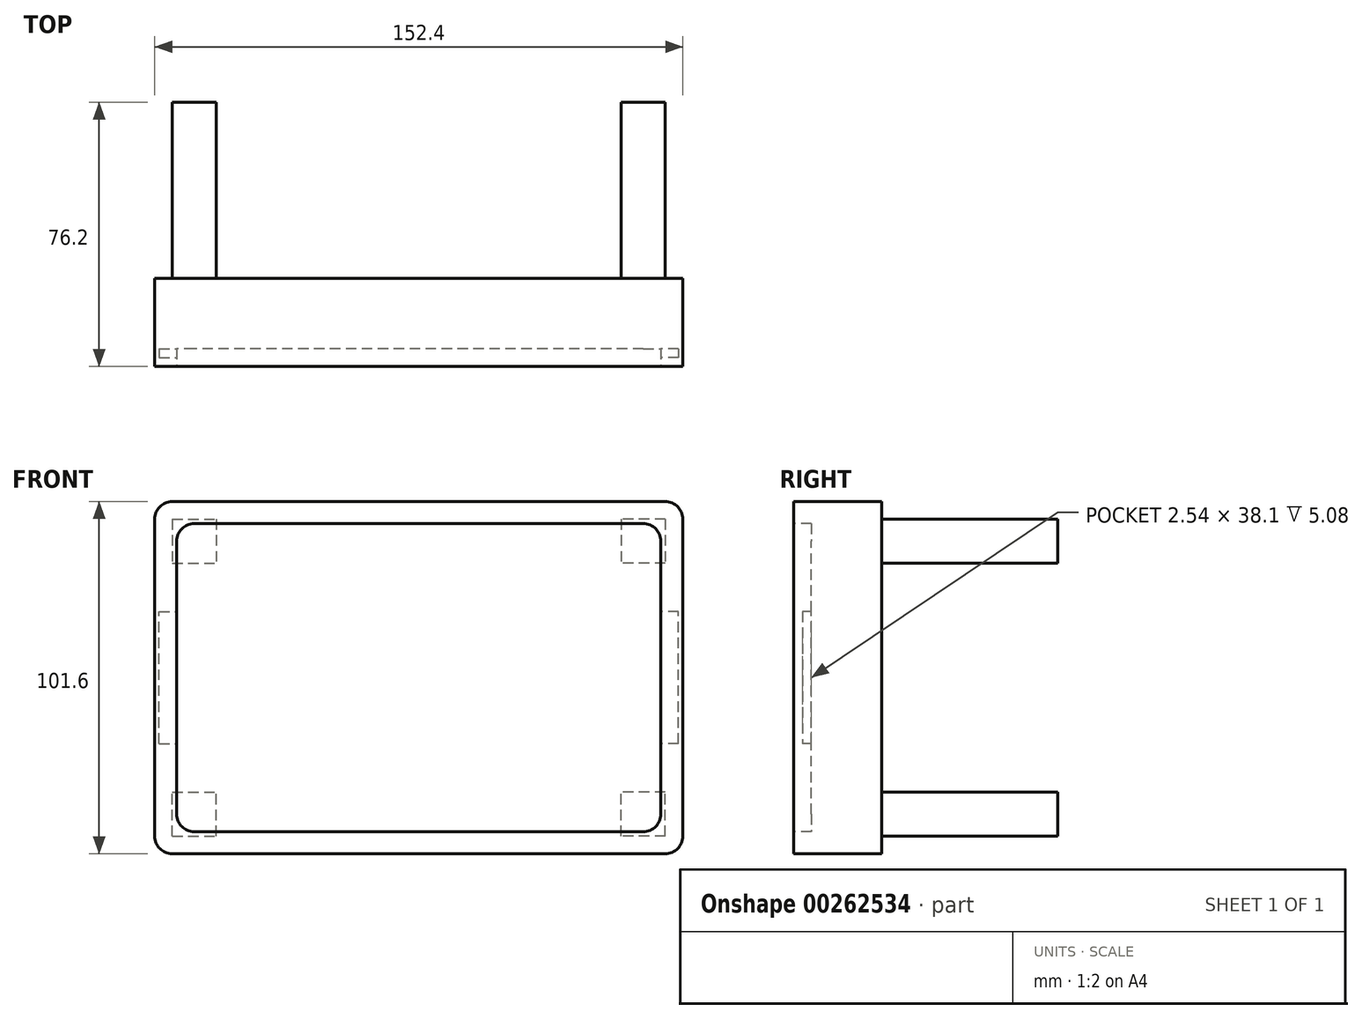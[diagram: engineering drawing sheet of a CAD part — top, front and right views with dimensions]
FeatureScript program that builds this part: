
annotation { "Feature Type Name" : "Feature", "Feature Type Description" : "" }
export const myFeature = defineFeature(function(context is Context, id is Id, definition is map)
    precondition{}
    {
        {
            var Q0;
            Q0=qCreatedBy(makeId("Front.planeOp"),FACE);
            var sketch = newSketch(context, id + "F0", { "sketchPlane" : qUnion([Q0])});
            skLineSegment(sketch, "E0.bottom", {"start": v(76.2, -50.8) * mm, "end": v(-76.2, -50.8) * mm});
            skLineSegment(sketch, "E0.top", {"start": v(76.2, 50.8) * mm, "end": v(-76.2, 50.8) * mm});
            skLineSegment(sketch, "E0.left", {"start": v(76.2, -50.8) * mm, "end": v(76.2, 50.8) * mm});
            skLineSegment(sketch, "E0.right", {"start": v(-76.2, -50.8) * mm, "end": v(-76.2, 50.8) * mm});
            skPoint(sketch, "E0.middle", {"position": v(0, 0) * mm});
            skSolve(sketch);
        }
        {
            var Q0;
            Q0=makeQuery(id+"F0.imprint","IMPRINT",FACE,{"disambiguationData":[TD([[makeQuery(id+"F0.imprint","IMPRINT",EDGE,{"derivedFrom":sQuery(id+"F0.wireOp",EDGE,"E0.bottom")}),-1.0]])]});
            extrude(context, id + "F1", {"entities" : qUnion([Q0]), "endBound" : BoundingType.SYMMETRIC, "depth" : 25.4 * mm});
        }
        {
            var Q0;
            Q0=makeQuery(id+"F1.opExtrude","CAP_FACE",FACE,{"disambiguationData":[OSD([sQuery(id+"F0.wireOp",EDGE,"E0.bottom"),sQuery(id+"F0.wireOp",EDGE,"E0.top"),sQuery(id+"F0.wireOp",EDGE,"E0.left"),sQuery(id+"F0.wireOp",EDGE,"E0.right")])],"isStart":false});
            var sketch = newSketch(context, id + "F2", { "sketchPlane" : qUnion([Q0])});
            skLineSegment(sketch, "E1.bottom", {"start": v(69.85, -44.45) * mm, "end": v(-69.85, -44.45) * mm});
            skLineSegment(sketch, "E1.top", {"start": v(69.85, 44.45) * mm, "end": v(-69.85, 44.45) * mm});
            skLineSegment(sketch, "E1.left", {"start": v(69.85, -44.45) * mm, "end": v(69.85, 44.45) * mm});
            skLineSegment(sketch, "E1.right", {"start": v(-69.85, -44.45) * mm, "end": v(-69.85, 44.45) * mm});
            skPoint(sketch, "E1.middle", {"position": v(0, 0) * mm});
            skSolve(sketch);
        }
        {
            var Q0;
            Q0=makeQuery(id+"F2.imprint","IMPRINT",FACE,{"disambiguationData":[TD([[makeQuery(id+"F2.imprint","IMPRINT",EDGE,{"derivedFrom":sQuery(id+"F2.wireOp",EDGE,"E1.bottom")}),-1.0]])]});
            extrude(context, id + "F3", {"entities" : qUnion([Q0]), "operationType" : NewBodyOperationType.REMOVE, "oppositeDirection" : true, "depth" : 5.08 * mm});
        }
        {
            var Q0;
            Q0=makeQuery(id+"F3.boolean.opBoolean","COPY",EDGE,{"derivedFrom":makeQuery(id+"F3.opExtrude","SWEPT_EDGE",EDGE,{"disambiguationData":[OSD([sQuery(id+"F2.wireOp",EDGE,"E1.bottom"),sQuery(id+"F2.wireOp",EDGE,"E1.right")])]})});
            var Q1;
            Q1=makeQuery(id+"F3.boolean.opBoolean","COPY",EDGE,{"derivedFrom":makeQuery(id+"F3.opExtrude","SWEPT_EDGE",EDGE,{"disambiguationData":[OSD([sQuery(id+"F2.wireOp",EDGE,"E1.bottom"),sQuery(id+"F2.wireOp",EDGE,"E1.left")])]})});
            var Q2;
            Q2=makeQuery(id+"F3.boolean.opBoolean","COPY",EDGE,{"derivedFrom":makeQuery(id+"F3.opExtrude","SWEPT_EDGE",EDGE,{"disambiguationData":[OSD([sQuery(id+"F2.wireOp",EDGE,"E1.top"),sQuery(id+"F2.wireOp",EDGE,"E1.left")])]})});
            var Q3;
            Q3=makeQuery(id+"F3.boolean.opBoolean","COPY",EDGE,{"derivedFrom":makeQuery(id+"F3.opExtrude","SWEPT_EDGE",EDGE,{"disambiguationData":[OSD([sQuery(id+"F2.wireOp",EDGE,"E1.top"),sQuery(id+"F2.wireOp",EDGE,"E1.right")])]})});
            var Q4;
            Q4=makeQuery(id+"F1.opExtrude","SWEPT_EDGE",EDGE,{"disambiguationData":[OSD([sQuery(id+"F0.wireOp",EDGE,"E0.top"),sQuery(id+"F0.wireOp",EDGE,"E0.right")])]});
            var Q5;
            Q5=makeQuery(id+"F1.opExtrude","SWEPT_EDGE",EDGE,{"disambiguationData":[OSD([sQuery(id+"F0.wireOp",EDGE,"E0.bottom"),sQuery(id+"F0.wireOp",EDGE,"E0.right")])]});
            var Q6;
            Q6=makeQuery(id+"F1.opExtrude","SWEPT_EDGE",EDGE,{"disambiguationData":[OSD([sQuery(id+"F0.wireOp",EDGE,"E0.top"),sQuery(id+"F0.wireOp",EDGE,"E0.left")])]});
            var Q7;
            Q7=makeQuery(id+"F1.opExtrude","SWEPT_EDGE",EDGE,{"disambiguationData":[OSD([sQuery(id+"F0.wireOp",EDGE,"E0.bottom"),sQuery(id+"F0.wireOp",EDGE,"E0.left")])]});
            fillet(context, id + "F4", {"entities" : qUnion([Q0, Q1, Q2, Q3, Q4, Q5, Q6, Q7]), "radius" : 5.08 * mm, "tangentPropagation" : true, "allowEdgeOverflow" : false});
        }
        {
            var Q0;
            Q0=makeQuery(id+"F3.boolean.opBoolean","COPY",FACE,{"derivedFrom":makeQuery(id+"F3.opExtrude","SWEPT_FACE",FACE,{"disambiguationData":[OSD([sQuery(id+"F2.wireOp",EDGE,"E1.right")])]})});
            var sketch = newSketch(context, id + "F5", { "sketchPlane" : qUnion([Q0])});
            skLineSegment(sketch, "E2.bottom", {"start": v(-7.62, 19.05) * mm, "end": v(-10.16, 19.05) * mm});
            skLineSegment(sketch, "E2.top", {"start": v(-7.62, -19.05) * mm, "end": v(-10.16, -19.05) * mm});
            skLineSegment(sketch, "E2.left", {"start": v(-7.62, 19.05) * mm, "end": v(-7.62, -19.05) * mm});
            skLineSegment(sketch, "E2.right", {"start": v(-10.16, 19.05) * mm, "end": v(-10.16, -19.05) * mm});
            skLineSegment(sketch, "E3", {"start": v(-7.62, -39.37) * mm, "end": v(-7.62, -19.05) * mm});
            skLineSegment(sketch, "E4", {"start": v(-7.62, 39.37) * mm, "end": v(-7.62, 19.05) * mm});
            skSolve(sketch);
        }
        {
            var Q0;
            Q0=makeQuery(id+"F5.imprint","IMPRINT",FACE,{"disambiguationData":[TD([[makeQuery(id+"F5.imprint","IMPRINT",EDGE,{"derivedFrom":sQuery(id+"F5.wireOp",EDGE,"E2.bottom")}),1.0]])]});
            extrude(context, id + "F6", {"entities" : qUnion([Q0]), "operationType" : NewBodyOperationType.REMOVE, "oppositeDirection" : true, "depth" : 5.08 * mm});
        }
        {
            var Q0;
            Q0=makeQuery(id+"F3.boolean.opBoolean","COPY",FACE,{"derivedFrom":makeQuery(id+"F3.opExtrude","SWEPT_FACE",FACE,{"disambiguationData":[OSD([sQuery(id+"F2.wireOp",EDGE,"E1.left")])]})});
            var sketch = newSketch(context, id + "F7", { "sketchPlane" : qUnion([Q0])});
            skLineSegment(sketch, "E5", {"start": v(7.62, 39.37) * mm, "end": v(7.62, 19.05) * mm});
            skLineSegment(sketch, "E6", {"start": v(7.62, -39.37) * mm, "end": v(7.62, -19.05) * mm});
            skLineSegment(sketch, "E7.bottom", {"start": v(7.62, 19.05) * mm, "end": v(10.16, 19.05) * mm});
            skLineSegment(sketch, "E7.top", {"start": v(7.62, -19.05) * mm, "end": v(10.16, -19.05) * mm});
            skLineSegment(sketch, "E7.left", {"start": v(7.62, 19.05) * mm, "end": v(7.62, -19.05) * mm});
            skLineSegment(sketch, "E7.right", {"start": v(10.16, 19.05) * mm, "end": v(10.16, -19.05) * mm});
            skSolve(sketch);
        }
        {
            var Q0;
            Q0=makeQuery(id+"F7.imprint","IMPRINT",FACE,{"disambiguationData":[TD([[makeQuery(id+"F7.imprint","IMPRINT",EDGE,{"derivedFrom":sQuery(id+"F7.wireOp",EDGE,"E7.bottom")}),-1.0]])]});
            extrude(context, id + "F8", {"entities" : qUnion([Q0]), "operationType" : NewBodyOperationType.REMOVE, "oppositeDirection" : true, "depth" : 5.08 * mm});
        }
        {
            var Q0;
            Q0=makeQuery(id+"F1.opExtrude","CAP_FACE",FACE,{"disambiguationData":[OSD([sQuery(id+"F0.wireOp",EDGE,"E0.bottom"),sQuery(id+"F0.wireOp",EDGE,"E0.top"),sQuery(id+"F0.wireOp",EDGE,"E0.left"),sQuery(id+"F0.wireOp",EDGE,"E0.right")])],"isStart":true});
            var sketch = newSketch(context, id + "F9", { "sketchPlane" : qUnion([Q0])});
            skLineSegment(sketch, "E8", {"start": v(71.12, 50.8) * mm, "end": v(71.12, 45.72) * mm});
            skLineSegment(sketch, "E9", {"start": v(71.12, -50.8) * mm, "end": v(71.12, -45.72) * mm});
            skLineSegment(sketch, "E10", {"start": v(-71.12, 50.8) * mm, "end": v(-71.12, 45.72) * mm});
            skLineSegment(sketch, "E11", {"start": v(-71.12, -50.8) * mm, "end": v(-71.12, -45.72) * mm});
            skLineSegment(sketch, "E12.bottom", {"start": v(71.12, 45.72) * mm, "end": v(58.42, 45.72) * mm});
            skLineSegment(sketch, "E12.top", {"start": v(71.12, 33.02) * mm, "end": v(58.42, 33.02) * mm});
            skLineSegment(sketch, "E12.left", {"start": v(71.12, 45.72) * mm, "end": v(71.12, 33.02) * mm});
            skLineSegment(sketch, "E12.right", {"start": v(58.42, 45.72) * mm, "end": v(58.42, 33.02) * mm});
            skLineSegment(sketch, "E13.bottom", {"start": v(71.12, -45.72) * mm, "end": v(58.42, -45.72) * mm});
            skLineSegment(sketch, "E13.top", {"start": v(71.12, -33.02) * mm, "end": v(58.42, -33.02) * mm});
            skLineSegment(sketch, "E13.left", {"start": v(71.12, -45.72) * mm, "end": v(71.12, -33.02) * mm});
            skLineSegment(sketch, "E13.right", {"start": v(58.42, -45.72) * mm, "end": v(58.42, -33.02) * mm});
            skLineSegment(sketch, "E14.bottom", {"start": v(-71.12, 45.72) * mm, "end": v(-58.42, 45.72) * mm});
            skLineSegment(sketch, "E14.top", {"start": v(-71.12, 33.02) * mm, "end": v(-58.42, 33.02) * mm});
            skLineSegment(sketch, "E14.left", {"start": v(-71.12, 45.72) * mm, "end": v(-71.12, 33.02) * mm});
            skLineSegment(sketch, "E14.right", {"start": v(-58.42, 45.72) * mm, "end": v(-58.42, 33.02) * mm});
            skLineSegment(sketch, "E15.bottom", {"start": v(-71.12, -45.72) * mm, "end": v(-58.42, -45.72) * mm});
            skLineSegment(sketch, "E15.top", {"start": v(-71.12, -33.02) * mm, "end": v(-58.42, -33.02) * mm});
            skLineSegment(sketch, "E15.left", {"start": v(-71.12, -45.72) * mm, "end": v(-71.12, -33.02) * mm});
            skLineSegment(sketch, "E15.right", {"start": v(-58.42, -45.72) * mm, "end": v(-58.42, -33.02) * mm});
            skSolve(sketch);
        }
        {
            var Q0;
            Q0=makeQuery(id+"F9.imprint","IMPRINT",FACE,{"disambiguationData":[TD([[makeQuery(id+"F9.imprint","IMPRINT",EDGE,{"derivedFrom":sQuery(id+"F9.wireOp",EDGE,"E12.bottom")}),1.0]])]});
            var Q1;
            Q1=makeQuery(id+"F9.imprint","IMPRINT",FACE,{"disambiguationData":[TD([[makeQuery(id+"F9.imprint","IMPRINT",EDGE,{"derivedFrom":sQuery(id+"F9.wireOp",EDGE,"E13.bottom")}),-1.0]])]});
            var Q2;
            Q2=makeQuery(id+"F9.imprint","IMPRINT",FACE,{"disambiguationData":[TD([[makeQuery(id+"F9.imprint","IMPRINT",EDGE,{"derivedFrom":sQuery(id+"F9.wireOp",EDGE,"E14.bottom")}),-1.0]])]});
            var Q3;
            Q3=makeQuery(id+"F9.imprint","IMPRINT",FACE,{"disambiguationData":[TD([[makeQuery(id+"F9.imprint","IMPRINT",EDGE,{"derivedFrom":sQuery(id+"F9.wireOp",EDGE,"E15.bottom")}),1.0]])]});
            extrude(context, id + "F10", {"entities" : qUnion([Q0, Q1, Q2, Q3]), "operationType" : NewBodyOperationType.ADD, "depth" : 50.8 * mm});
        }
    });
